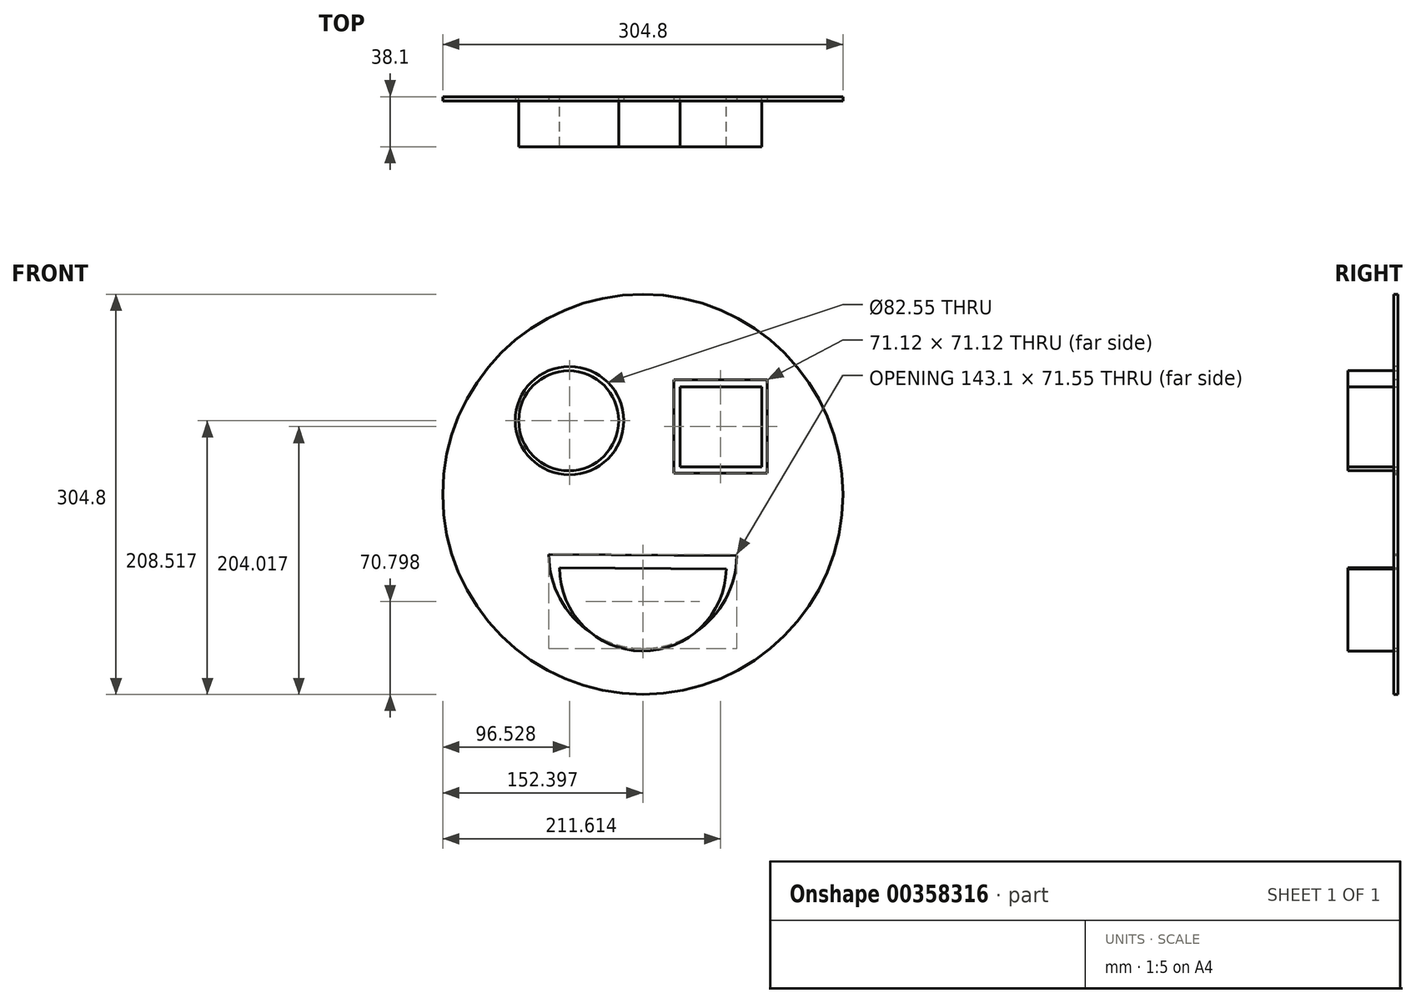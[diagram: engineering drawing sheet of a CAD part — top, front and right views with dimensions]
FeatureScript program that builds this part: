
annotation { "Feature Type Name" : "Feature", "Feature Type Description" : "" }
export const myFeature = defineFeature(function(context is Context, id is Id, definition is map)
    precondition{}
    {
        {
            var Q0;
            Q0=qCreatedBy(makeId("Front.planeOp"),FACE);
            var sketch = newSketch(context, id + "F0", { "sketchPlane" : qUnion([Q0])});
            skCircle(sketch, "E0", {"center": v(0, 0) * mm, "radius": 152.4 * mm});
            skSolve(sketch);
        }
        {
            var Q0;
            Q0=makeQuery(id+"F0.imprint","IMPRINT",FACE,{"disambiguationData":[TD([[makeQuery(id+"F0.imprint","IMPRINT",EDGE,{"derivedFrom":sQuery(id+"F0.wireOp",EDGE,"E0")}),1.0]])]});
            extrude(context, id + "F1", {"entities" : qUnion([Q0]), "depth" : 3.17 * mm});
        }
        {
            var Q0;
            Q0=makeQuery(id+"F1.opExtrude","CAP_FACE",FACE,{"disambiguationData":[OSD([sQuery(id+"F0.wireOp",EDGE,"E0")])],"isStart":false});
            var sketch = newSketch(context, id + "F2", { "sketchPlane" : qUnion([Q0])});
            skCircle(sketch, "E1", {"center": v(-55.87, 56.12) * mm, "radius": 41.28 * mm});
            skSolve(sketch);
        }
        {
            var Q0;
            Q0=makeQuery(id+"F1.opExtrude","CAP_FACE",FACE,{"disambiguationData":[OSD([sQuery(id+"F0.wireOp",EDGE,"E0")])],"isStart":false});
            var sketch = newSketch(context, id + "F3", { "sketchPlane" : qUnion([Q0])});
            skLineSegment(sketch, "E2.bottom", {"start": v(94.77, 87.18) * mm, "end": v(23.65, 87.18) * mm});
            skLineSegment(sketch, "E2.top", {"start": v(94.77, 16.06) * mm, "end": v(23.65, 16.06) * mm});
            skLineSegment(sketch, "E2.left", {"start": v(94.77, 87.18) * mm, "end": v(94.77, 16.06) * mm});
            skLineSegment(sketch, "E2.right", {"start": v(23.65, 87.18) * mm, "end": v(23.65, 16.06) * mm});
            skPoint(sketch, "E2.middle", {"position": v(59.21, 51.62) * mm});
            skSolve(sketch);
        }
        {
            var Q0;
            Q0 = qSketchRegion(id + "F3", true);
            extrude(context, id + "F4", {"entities" : qUnion([Q0]), "operationType" : NewBodyOperationType.REMOVE, "oppositeDirection" : true, "depth" : 25.4 * mm});
        }
        {
            var Q0;
            Q0=makeQuery(id+"F1.opExtrude","CAP_FACE",FACE,{"disambiguationData":[OSD([sQuery(id+"F0.wireOp",EDGE,"E0")])],"isStart":false});
            var sketch = newSketch(context, id + "F5", { "sketchPlane" : qUnion([Q0])});
            skArc(sketch, "E3", {"start": v(-71.56, -45.83) * mm, "mid": v(-0.5, -117.38) * mm, "end": v(71.55, -46.8) * mm});
            skLineSegment(sketch, "E4", {"start": v(-71.56, -45.83) * mm, "end": v(71.55, -46.8) * mm});
            skSolve(sketch);
        }
        {
            var Q0;
            Q0=makeQuery(id+"F5.imprint","IMPRINT",FACE,{"disambiguationData":[TD([[makeQuery(id+"F5.imprint","IMPRINT",EDGE,{"derivedFrom":sQuery(id+"F5.wireOp",EDGE,"E3")}),1.0]])]});
            extrude(context, id + "F6", {"entities" : qUnion([Q0]), "operationType" : NewBodyOperationType.REMOVE, "oppositeDirection" : true, "depth" : 25.4 * mm});
        }
        {
            var Q0;
            Q0 = qSketchRegion(id + "F2", true);
            extrude(context, id + "F7", {"entities" : qUnion([Q0]), "operationType" : NewBodyOperationType.REMOVE, "oppositeDirection" : true, "depth" : 25.4 * mm});
        }
        {
            var Q0;
            Q0=qCreatedBy(makeId("Front.planeOp"),FACE);
            var sketch = newSketch(context, id + "F8", { "sketchPlane" : qUnion([Q0])});
            skCircle(sketch, "E5", {"center": v(-56.45, 56.1) * mm, "radius": 38.1 * mm});
            skSolve(sketch);
        }
        {
            var Q0;
            Q0=makeQuery(id+"F8.imprint","IMPRINT",FACE,{"disambiguationData":[TD([[makeQuery(id+"F8.imprint","IMPRINT",EDGE,{"derivedFrom":sQuery(id+"F8.wireOp",EDGE,"E5")}),1.0]])]});
            extrude(context, id + "F9", {"entities" : qUnion([Q0]), "depth" : 38.1 * mm});
        }
        {
            var Q0;
            Q0=qCreatedBy(makeId("Front.planeOp"),FACE);
            var sketch = newSketch(context, id + "F10", { "sketchPlane" : qUnion([Q0])});
            skLineSegment(sketch, "E6.bottom", {"start": v(28.43, 20.83) * mm, "end": v(90.66, 20.83) * mm});
            skLineSegment(sketch, "E6.top", {"start": v(28.43, 81.79) * mm, "end": v(90.66, 81.79) * mm});
            skLineSegment(sketch, "E6.left", {"start": v(28.43, 20.83) * mm, "end": v(28.43, 81.79) * mm});
            skLineSegment(sketch, "E6.right", {"start": v(90.66, 20.83) * mm, "end": v(90.66, 81.79) * mm});
            skSolve(sketch);
        }
        {
            var Q0;
            Q0=makeQuery(id+"F10.imprint","IMPRINT",FACE,{"disambiguationData":[TD([[makeQuery(id+"F10.imprint","IMPRINT",EDGE,{"derivedFrom":sQuery(id+"F10.wireOp",EDGE,"E6.bottom")}),1.0]])]});
            extrude(context, id + "F11", {"entities" : qUnion([Q0]), "depth" : 38.1 * mm});
        }
        {
            var Q0;
            Q0=qCreatedBy(makeId("Front.planeOp"),FACE);
            var sketch = newSketch(context, id + "F12", { "sketchPlane" : qUnion([Q0])});
            skArc(sketch, "E7", {"start": v(-63.5, -55.83) * mm, "mid": v(-0.5, -119.33) * mm, "end": v(63.5, -56.84) * mm});
            skLineSegment(sketch, "E8", {"start": v(-63.5, -55.83) * mm, "end": v(63.5, -56.84) * mm});
            skSolve(sketch);
        }
        {
            var Q0;
            Q0 = qSketchRegion(id + "F12", true);
            extrude(context, id + "F13", {"entities" : qUnion([Q0]), "depth" : 38.1 * mm});
        }
    });
